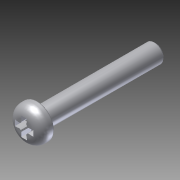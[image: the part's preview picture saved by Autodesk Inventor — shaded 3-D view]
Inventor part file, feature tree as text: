
AUTODESK INVENTOR PART (.ipt)
format: ipt  version: 2011 SP1 (Build 150282100, 282)  size: 135,680 bytes
history: native  units: in
note: dims shown in document units (in); Inventor stores cm internally (conversion verified against a paired STEP export)
features: other x14, sketch x2, revolve x1, extrude x1
ambient origin geometry x8: Origin, YZ Plane, XZ Plane, XY Plane, X Axis, Y Axis, Z Axis, Center Point
bodies: Solid1 (feature_tree)
feature tree (18):
  revolve  "Revolution1"  [1 undecoded]
  extrude  "Extrusion1"  [1 undecoded]
  other  "IP1_XY"
  other  "IP1_YZ"
  other  "IP1_ZX"
  other  "IP1_X"
  other  "IP1_Y"
  other  "IP1_Z"
  other  "IP1_Center"
  other  "IP3_XY"
  other  "IP3_YZ"
  other  "IP3_ZX"
  other  "IP3_X"
  other  "IP3_Y"
  other  "IP3_Z"
  other  "IP3_Center"
  sketch  "Sketch_1"  dims[d0=360.0deg d1=0.06in d2=0.0in]
  sketch  "Sketch_2"
note: 2 required parameter values undecoded (feature->parameter linkage not recoverable at this tier; creation-order binding heuristic only, values carry confidence <= 0.55)